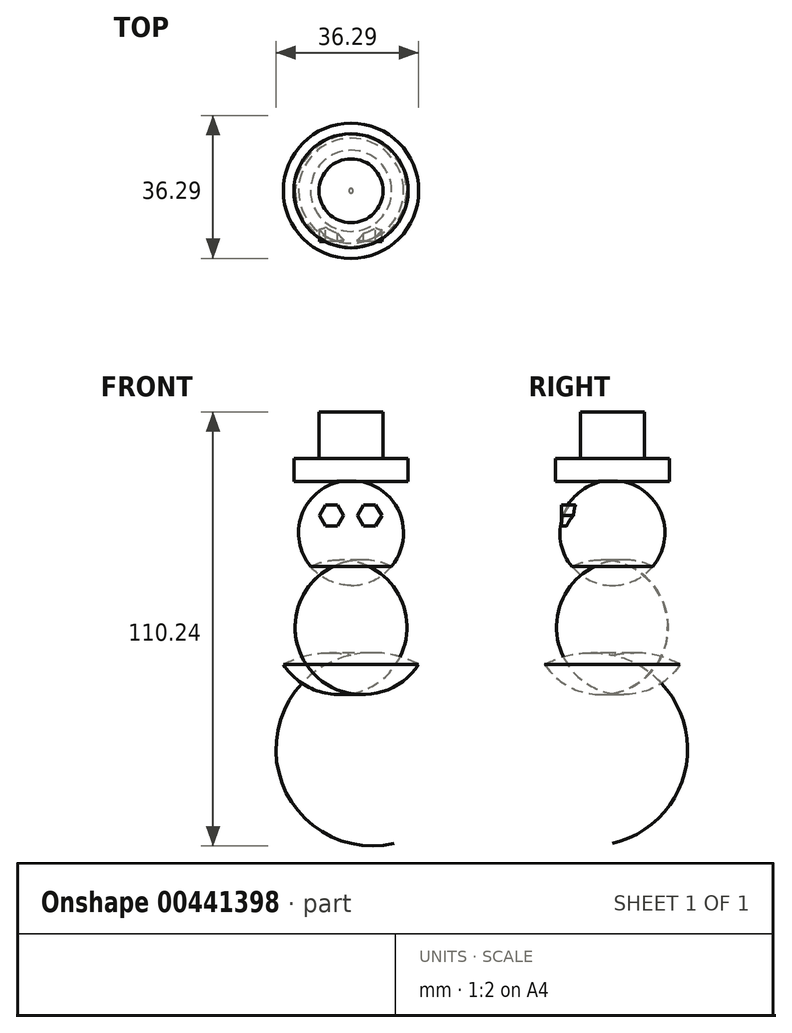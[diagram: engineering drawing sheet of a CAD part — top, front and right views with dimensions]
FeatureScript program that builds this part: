
annotation { "Feature Type Name" : "Feature", "Feature Type Description" : "" }
export const myFeature = defineFeature(function(context is Context, id is Id, definition is map)
    precondition{}
    {
        {
            var Q0;
            Q0=qCreatedBy(makeId("Front.planeOp"),FACE);
            var sketch = newSketch(context, id + "F0", { "sketchPlane" : qUnion([Q0])});
            skLineSegment(sketch, "E0", {"start": v(0, 54.17) * mm, "end": v(0, 27.48) * mm, "construction": true});
            skArc(sketch, "E1", {"start": v(0, 54.17) * mm, "mid": v(-13.34, 40.83) * mm, "end": v(0, 27.48) * mm});
            skLineSegment(sketch, "E2", {"start": v(0, 54.17) * mm, "end": v(0, 71.57) * mm});
            skLineSegment(sketch, "E3", {"start": v(0, 71.57) * mm, "end": v(-8.12, 71.57) * mm});
            skLineSegment(sketch, "E4", {"start": v(-8.12, 71.57) * mm, "end": v(-8.12, 59.78) * mm});
            skLineSegment(sketch, "E5", {"start": v(-8.12, 59.78) * mm, "end": v(-14.5, 59.78) * mm});
            skLineSegment(sketch, "E6", {"start": v(-14.5, 59.78) * mm, "end": v(-14.5, 53.88) * mm});
            skLineSegment(sketch, "E7", {"start": v(-14.5, 53.88) * mm, "end": v(0, 54.17) * mm});
            skLineSegment(sketch, "E8", {"start": v(0, 33.77) * mm, "end": v(0, 0) * mm, "construction": true});
            skArc(sketch, "E9", {"start": v(0, 33.77) * mm, "mid": v(-20.05, 16.88) * mm, "end": v(0, 0) * mm});
            skLineSegment(sketch, "E10", {"start": v(0, 9.8) * mm, "end": v(0, -38.06) * mm, "construction": true});
            skArc(sketch, "E11", {"start": v(0, 9.8) * mm, "mid": v(-30, -14.13) * mm, "end": v(0, -38.06) * mm});
            skLineSegment(sketch, "E12", {"start": v(0, 71.57) * mm, "end": v(0, -38.06) * mm, "construction": true});
            skLineSegment(sketch, "E13", {"start": v(0, -38.06) * mm, "end": v(0, 71.57) * mm});
            skSolve(sketch);
        }
        {
            var Q0;
            {var subQ0=sQuery(id+"F0.wireOp",EDGE,"E3");Q0=makeQuery(id+"F0.imprint","IMPRINT",FACE,{"disambiguationData":[TD([[makeQuery(id+"F0.imprint","IMPRINT",EDGE,{"derivedFrom":subQ0}),1.0]])]});}
            var Q1;
            {var subQ0=sQuery(id+"F0.wireOp",EDGE,"E7");var subQ1=sQuery(id+"F0.wireOp",EDGE,"E1");var subQ2=makeQuery(id+"F0.imprint","INTERSECT",VERTEX,{"derivedFrom":[subQ1,subQ0]});Q1=makeQuery(id+"F0.imprint","IMPRINT",FACE,{"disambiguationData":[TD([[makeQuery(id+"F0.imprint","IMPRINT",EDGE,{"disambiguationData":[TD([[subQ2,-1.0]])],"derivedFrom":subQ1}),1.0]])]});}
            var Q2;
            {var subQ0=sQuery(id+"F0.wireOp",EDGE,"E13");var subQ1=sQuery(id+"F0.wireOp",EDGE,"E1");var subQ2=makeQuery(id+"F0.imprint","INTERSECT",VERTEX,{"derivedFrom":[subQ1,subQ0]});Q2=makeQuery(id+"F0.imprint","IMPRINT",FACE,{"disambiguationData":[TD([[makeQuery(id+"F0.imprint","IMPRINT",EDGE,{"disambiguationData":[TD([[subQ2,1.0]])],"derivedFrom":subQ1}),-1.0]])]});}
            var Q3;
            {var subQ0=sQuery(id+"F0.wireOp",EDGE,"E13");var subQ1=sQuery(id+"F0.wireOp",EDGE,"E9");var subQ2=makeQuery(id+"F0.imprint","INTERSECT",VERTEX,{"disambiguationData":[OD(1.0)],"derivedFrom":[subQ1,subQ0]});Q3=makeQuery(id+"F0.imprint","IMPRINT",FACE,{"disambiguationData":[TD([[makeQuery(id+"F0.imprint","IMPRINT",EDGE,{"disambiguationData":[TD([[subQ2,1.0]])],"derivedFrom":subQ1}),-1.0]])]});}
            var Q4;
            Q4=sQuery(id+"F0.wireOp",EDGE,"E12");
            revolve(context, id + "F1", {"entities" : qUnion([Q0, Q1, Q2, Q3]), "axis" : qUnion([Q4]), "revolveType" : RevolveType.FULL});
        }
        {
            var Q0;
            Q0=qCreatedBy(makeId("Front.planeOp"),FACE);
            cPlane(context, id + "F2", {"entities" : qUnion([Q0]), "cplaneType" : CPlaneType.OFFSET, "offset" : 6.35 * mm, "width" : 152.4 * mm, "height" : 152.4 * mm});
        }
        {
            var Q0;
            Q0=qCreatedBy(id+"F2.planeOp",FACE);
            var sketch = newSketch(context, id + "F3", { "sketchPlane" : qUnion([Q0])});
            skCircle(sketch, "E14.cCircle", {"center": v(-4.93, 45.31) * mm, "radius": 2.65 * mm, "construction": true});
            skLineSegment(sketch, "E14.0", {"start": v(-3.4, 42.66) * mm, "end": v(-6.46, 42.66) * mm});
            skLineSegment(sketch, "E14.1", {"start": v(-6.46, 42.66) * mm, "end": v(-8, 45.31) * mm});
            skLineSegment(sketch, "E14.2", {"start": v(-8, 45.31) * mm, "end": v(-6.46, 47.97) * mm});
            skLineSegment(sketch, "E14.3", {"start": v(-6.46, 47.97) * mm, "end": v(-3.4, 47.97) * mm});
            skLineSegment(sketch, "E14.4", {"start": v(-3.4, 47.97) * mm, "end": v(-1.86, 45.31) * mm});
            skLineSegment(sketch, "E14.5", {"start": v(-1.86, 45.31) * mm, "end": v(-3.4, 42.66) * mm});
            skPoint(sketch, "E14.0.midPoint", {"position": v(-4.93, 42.66) * mm});
            skCircle(sketch, "E15.cCircle", {"center": v(4.74, 45.31) * mm, "radius": 2.65 * mm, "construction": true});
            skLineSegment(sketch, "E15.0", {"start": v(6.27, 42.66) * mm, "end": v(3.2, 42.66) * mm});
            skLineSegment(sketch, "E15.1", {"start": v(3.2, 42.66) * mm, "end": v(1.67, 45.31) * mm});
            skLineSegment(sketch, "E15.2", {"start": v(1.67, 45.31) * mm, "end": v(3.2, 47.97) * mm});
            skLineSegment(sketch, "E15.3", {"start": v(3.2, 47.97) * mm, "end": v(6.27, 47.97) * mm});
            skLineSegment(sketch, "E15.4", {"start": v(6.27, 47.97) * mm, "end": v(7.8, 45.31) * mm});
            skLineSegment(sketch, "E15.5", {"start": v(7.8, 45.31) * mm, "end": v(6.27, 42.66) * mm});
            skPoint(sketch, "E15.0.midPoint", {"position": v(4.74, 42.66) * mm});
            skSolve(sketch);
        }
        {
            var Q0;
            Q0 = qSketchRegion(id + "F3", true);
            extrude(context, id + "F4", {"entities" : qUnion([Q0]), "operationType" : NewBodyOperationType.ADD, "depth" : 6.6 * mm});
        }
    });
